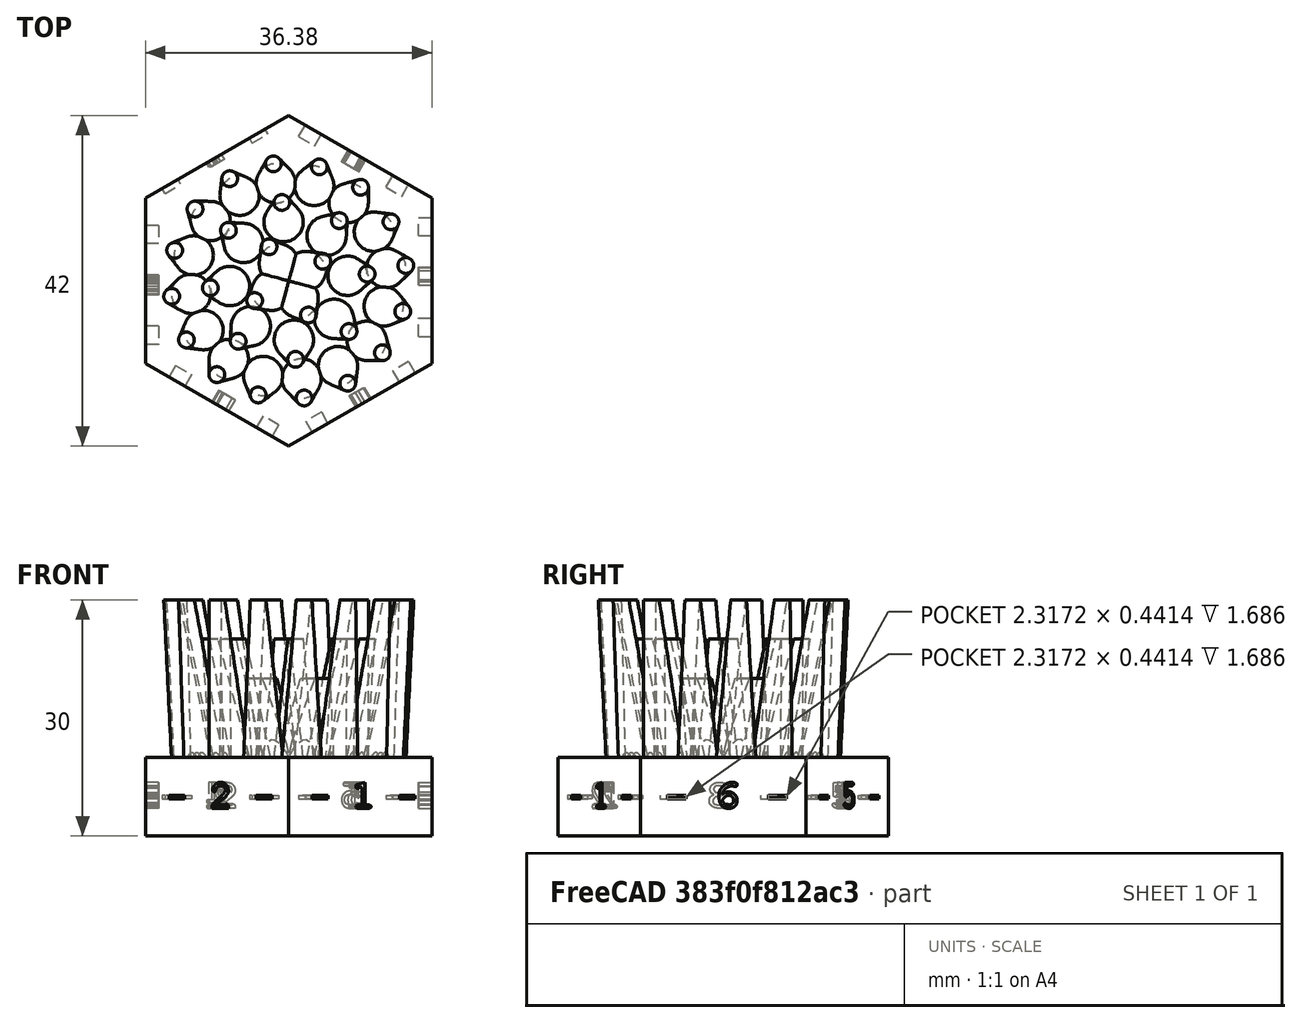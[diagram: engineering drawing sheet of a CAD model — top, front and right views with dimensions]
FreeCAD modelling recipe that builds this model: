
FCSTD DOCUMENT  (FreeCAD 0.16R6560 (Git))
Label: supportScan
License: All rights reserved
LicenseURL: http://fr.wikipedia.org/wiki/<copyright redacted>
objects: Sketcher::SketchObject×7, PartDesign::Pad×7, Part::Part2DObjectPython×6, Part::Cut×6, Part::Loft×3, Part::FeaturePython×3, Part::MultiFuse×1
note: 40 computed .brp shape members not serialized (recipe doc carries the construction recipe); baked Part::Feature solids carry a one-line shape summary decoded from their .brp

FEATURE [Sketcher::SketchObject] Sketch
  sketch-geometry (1):
    g0: Circle CenterX=0 CenterY=12.5 CenterZ=0 NormalX=0 NormalY=0 NormalZ=1 Radius=2.5
  constraints (3):
    c: PointOnObject(g0,g-2)
    c: DistanceY(g-1,g0) = 12.5
    c: Radius(g0) = 2.5
FEATURE [Sketcher::SketchObject] Sketch001
  Placement = pos=(0,0,20) rot=(0,0,1;0rad)
  sketch-geometry (1):
    g0: Circle CenterX=0 CenterY=15 CenterZ=0 NormalX=0 NormalY=0 NormalZ=1 Radius=1
  constraints (3):
    c: PointOnObject(g0,g-2)
    c: DistanceY(g-1,g0) = 15
    c: Radius(g0) = 1
FEATURE [Part::Loft] Loft
  Closed = false
  Ruled = true
  Sections = -> [Sketch,Sketch001]
  Solid = true
FEATURE [Part::FeaturePython] Array  # Draft array (typed FeaturePython)
  Angle = 360
  ArrayType = 1
  Axis = (0,0,1)
  Base = -> Loft
  Center = (0,0,0)
  Fuse = true
  IntervalAxis = (0,0,0)
  IntervalX = (1,0,0)
  IntervalY = (0,1,0)
  IntervalZ = (0,0,0)
  NumberPolar = 16
  NumberX = 2
  NumberY = 2
  NumberZ = 1
FEATURE [Sketcher::SketchObject] Sketch002
  sketch-geometry (3):
    g0: Circle [constr] CenterX=0 CenterY=0 CenterZ=0 NormalX=0 NormalY=0 NormalZ=1 Radius=7.5
    g1: LineSegment [constr] StartX=-2.56515 StartY=7.04769 StartZ=0 EndX=0 EndY=0 EndZ=0
    g2: Circle CenterX=-2.56515 CenterY=7.04769 CenterZ=0 NormalX=0 NormalY=0 NormalZ=1 Radius=2.5
  constraints (9):
    c: PointOnObject(g0,g-1)
    c: PointOnObject(g0,g-2)
    c: Radius(g0) = 7.5
    c: PointOnObject(g1,g-1)
    c: PointOnObject(g1,g-2)
    c: PointOnObject(g1,g0)
    c: Angle(g-2,g1) = 0.349066
    c: Coincident(g2,g1)
    c: Radius(g2) = 2.5
FEATURE [Sketcher::SketchObject] Sketch003
  Placement = pos=(0,0,15) rot=(0,0,1;0rad)
  sketch-geometry (3):
    g0: Circle [constr] CenterX=0 CenterY=0 CenterZ=0 NormalX=0 NormalY=0 NormalZ=1 Radius=10
    g1: LineSegment [constr] StartX=-3.4202 StartY=9.39693 StartZ=0 EndX=0 EndY=0 EndZ=0
    g2: Circle CenterX=-3.4202 CenterY=9.39693 CenterZ=0 NormalX=0 NormalY=0 NormalZ=1 Radius=1
  constraints (9):
    c: PointOnObject(g0,g-1)
    c: PointOnObject(g0,g-2)
    c: Radius(g0) = 10
    c: PointOnObject(g1,g-1)
    c: PointOnObject(g1,g-2)
    c: PointOnObject(g1,g0)
    c: Angle(g-2,g1) = 0.349066
    c: Coincident(g2,g1)
    c: Radius(g2) = 1
FEATURE [Part::Loft] Loft001
  Closed = false
  Ruled = true
  Sections = -> [Sketch002,Sketch003]
  Solid = true
FEATURE [Part::FeaturePython] Array001  # Draft array (typed FeaturePython)
  Angle = 360
  ArrayType = 1
  Axis = (0,0,1)
  Base = -> Loft001
  Center = (0,0,0)
  Fuse = false
  IntervalAxis = (0,0,0)
  IntervalX = (1,0,0)
  IntervalY = (0,1,0)
  IntervalZ = (0,0,0)
  NumberPolar = 8
  NumberX = 2
  NumberY = 2
  NumberZ = 1
FEATURE [Sketcher::SketchObject] Sketch004
  sketch-geometry (1):
    g0: Circle CenterX=0 CenterY=2.5 CenterZ=0 NormalX=0 NormalY=0 NormalZ=1 Radius=2.5
  constraints (3):
    c: PointOnObject(g0,g-2)
    c: DistanceY(g-1,g0) = 2.5
    c: Radius(g0) = 2.5
FEATURE [Sketcher::SketchObject] Sketch005
  Placement = pos=(0,0,10) rot=(0,0,1;0rad)
  sketch-geometry (1):
    g0: Circle CenterX=0 CenterY=5 CenterZ=0 NormalX=0 NormalY=0 NormalZ=1 Radius=1
  constraints (3):
    c: PointOnObject(g0,g-2)
    c: DistanceY(g-1,g0) = 5
    c: Radius(g0) = 1
FEATURE [Part::Loft] Loft002
  Closed = false
  Ruled = true
  Sections = -> [Sketch004,Sketch005]
  Solid = true
FEATURE [Part::FeaturePython] Array002  # Draft array (typed FeaturePython)
  Angle = 360
  ArrayType = 1
  Axis = (0,0,1)
  Base = -> Loft002
  Center = (0,0,0)
  Fuse = true
  IntervalAxis = (0,0,0)
  IntervalX = (1,0,0)
  IntervalY = (0,1,0)
  IntervalZ = (0,0,0)
  NumberPolar = 4
  NumberX = 2
  NumberY = 2
  NumberZ = 1
FEATURE [Sketcher::SketchObject] Sketch006
  Placement = pos=(0,0,0) rot=(1,0,0;3.14159rad)
  sketch-geometry (7):
    g0: LineSegment StartX=-18.1865 StartY=-10.5 StartZ=0 EndX=2e-12 EndY=-21 EndZ=0
    g1: LineSegment StartX=2e-12 StartY=-21 StartZ=0 EndX=18.1865 EndY=-10.5 EndZ=0
    g2: LineSegment StartX=18.1865 StartY=-10.5 StartZ=0 EndX=18.1865 EndY=10.5 EndZ=0
    g3: LineSegment StartX=18.1865 StartY=10.5 StartZ=0 EndX=0 EndY=21 EndZ=0
    g4: LineSegment StartX=0 StartY=21 StartZ=0 EndX=-18.1865 EndY=10.5 EndZ=0
    g5: LineSegment StartX=-18.1865 StartY=10.5 StartZ=0 EndX=-18.1865 EndY=-10.5 EndZ=0
    g6: Circle [constr] CenterX=0 CenterY=0 CenterZ=0 NormalX=0 NormalY=0 NormalZ=1 Radius=21
  constraints (17):
    c: Coincident(g0,g1)
    c: Coincident(g1,g2)
    c: Coincident(g2,g3)
    c: Coincident(g3,g4)
    c: Coincident(g4,g5)
    c: Coincident(g5,g0)
    c: Equal(g0, g1-g5) x5
    c: PointOnObject(g0,g6)
    c: PointOnObject(g1,g6)
    c: PointOnObject(g2,g6)
    c: PointOnObject(g3,g6)
    c: PointOnObject(g4,g6)
    c: PointOnObject(g5,g6)
    c: PointOnObject(g6,g-1)
    c: PointOnObject(g6,g-2)
    c: Vertical(g2)
    c: Radius(g6) = 21
FEATURE [PartDesign::Pad] Pad
  Length = 10
  Length2 = 100
  Placement = pos=(0,0,0) rot=(1,0,0;3.14159rad)
  Sketch = -> Sketch006
  Type = 0
FEATURE [Part::MultiFuse] Fusion  label="supportScan001"
  Shapes = -> [Array,Pad,Array002,Array001]
FEATURE [Part::Part2DObjectPython] ShapeString  # Draft 2D object (typed FeaturePython)
  FontFile = <path>
  Placement = pos=(18.5,-7.5,-6.5) rot=(0.57735,0.57735,0.57735;2.0944rad)
  Size = 4
  String = - 1 -
  Tracking = 0
FEATURE [PartDesign::Pad] Pad001
  Length = 4
  Length2 = 100
  Midplane = true
  Placement = pos=(18.5,-7.5,-6.5) rot=(0.57735,0.57735,0.57735;2.0944rad)
  Sketch = -> ShapeString
  Type = 0
FEATURE [Part::Cut] Cut
  Base = -> Fusion
  Placement = pos=(0,0,0) rot=(0,0,1;1.0472rad)
  Tool = -> Pad001
FEATURE [Part::Part2DObjectPython] ShapeString001  # Draft 2D object (typed FeaturePython)
  FontFile = <path>
  Placement = pos=(18.5,-7.5,-6.5) rot=(0.57735,0.57735,0.57735;2.0944rad)
  Size = 4
  String = - 2 -
  Tracking = 0
FEATURE [PartDesign::Pad] Pad002
  Length = 4
  Length2 = 100
  Midplane = true
  Placement = pos=(18.5,-7.5,-6.5) rot=(0.57735,0.57735,0.57735;2.0944rad)
  Sketch = -> ShapeString001
  Type = 0
FEATURE [Part::Cut] Cut001
  Base = -> Cut
  Placement = pos=(0,0,0) rot=(0,0,1;1.0472rad)
  Tool = -> Pad002
FEATURE [Part::Part2DObjectPython] ShapeString002  # Draft 2D object (typed FeaturePython)
  FontFile = <path>
  Placement = pos=(18.5,-7.5,-6.5) rot=(0.57735,0.57735,0.57735;2.0944rad)
  Size = 4
  String = - 3 -
  Tracking = 0
FEATURE [PartDesign::Pad] Pad003
  Length = 4
  Length2 = 100
  Midplane = true
  Placement = pos=(18.5,-7.5,-6.5) rot=(0.57735,0.57735,0.57735;2.0944rad)
  Sketch = -> ShapeString002
  Type = 0
FEATURE [Part::Cut] Cut002
  Base = -> Cut001
  Placement = pos=(0,0,0) rot=(0,0,1;1.0472rad)
  Tool = -> Pad003
FEATURE [Part::Part2DObjectPython] ShapeString003  # Draft 2D object (typed FeaturePython)
  FontFile = <path>
  Placement = pos=(18.5,-7.5,-6.5) rot=(0.57735,0.57735,0.57735;2.0944rad)
  Size = 4
  String = - 4 -
  Tracking = 0
FEATURE [PartDesign::Pad] Pad004
  Length = 2
  Length2 = 100
  Midplane = true
  Placement = pos=(18.5,-7.5,-6.5) rot=(0.57735,0.57735,0.57735;2.0944rad)
  Sketch = -> ShapeString003
  Type = 0
FEATURE [Part::Cut] Cut003
  Base = -> Cut002
  Placement = pos=(0,0,0) rot=(0,0,1;1.0472rad)
  Tool = -> Pad004
FEATURE [Part::Part2DObjectPython] ShapeString004  # Draft 2D object (typed FeaturePython)
  FontFile = <path>
  Placement = pos=(18.5,-7.5,-6.5) rot=(0.57735,0.57735,0.57735;2.0944rad)
  Size = 4
  String = - 5 -
  Tracking = 0
FEATURE [PartDesign::Pad] Pad005
  Length = 4
  Length2 = 100
  Midplane = true
  Placement = pos=(18.5,-7.5,-6.5) rot=(0.57735,0.57735,0.57735;2.0944rad)
  Sketch = -> ShapeString004
  Type = 0
FEATURE [Part::Cut] Cut004
  Base = -> Cut003
  Placement = pos=(0,0,0) rot=(0,0,1;1.0472rad)
  Tool = -> Pad005
FEATURE [Part::Part2DObjectPython] ShapeString005  # Draft 2D object (typed FeaturePython)
  FontFile = <path>
  Placement = pos=(18.5,-7.5,-6.5) rot=(0.57735,0.57735,0.57735;2.0944rad)
  Size = 4
  String = - 6 -
  Tracking = 0
FEATURE [PartDesign::Pad] Pad006
  Length = 4
  Length2 = 100
  Midplane = true
  Placement = pos=(18.5,-7.5,-6.5) rot=(0.57735,0.57735,0.57735;2.0944rad)
  Sketch = -> ShapeString005
  Type = 0
FEATURE [Part::Cut] Cut005  label="supportScan002"
  Base = -> Cut004
  Tool = -> Pad006
note: 6 file-system paths scrubbed to <path> (originals preserved in the JSON sidecar)
